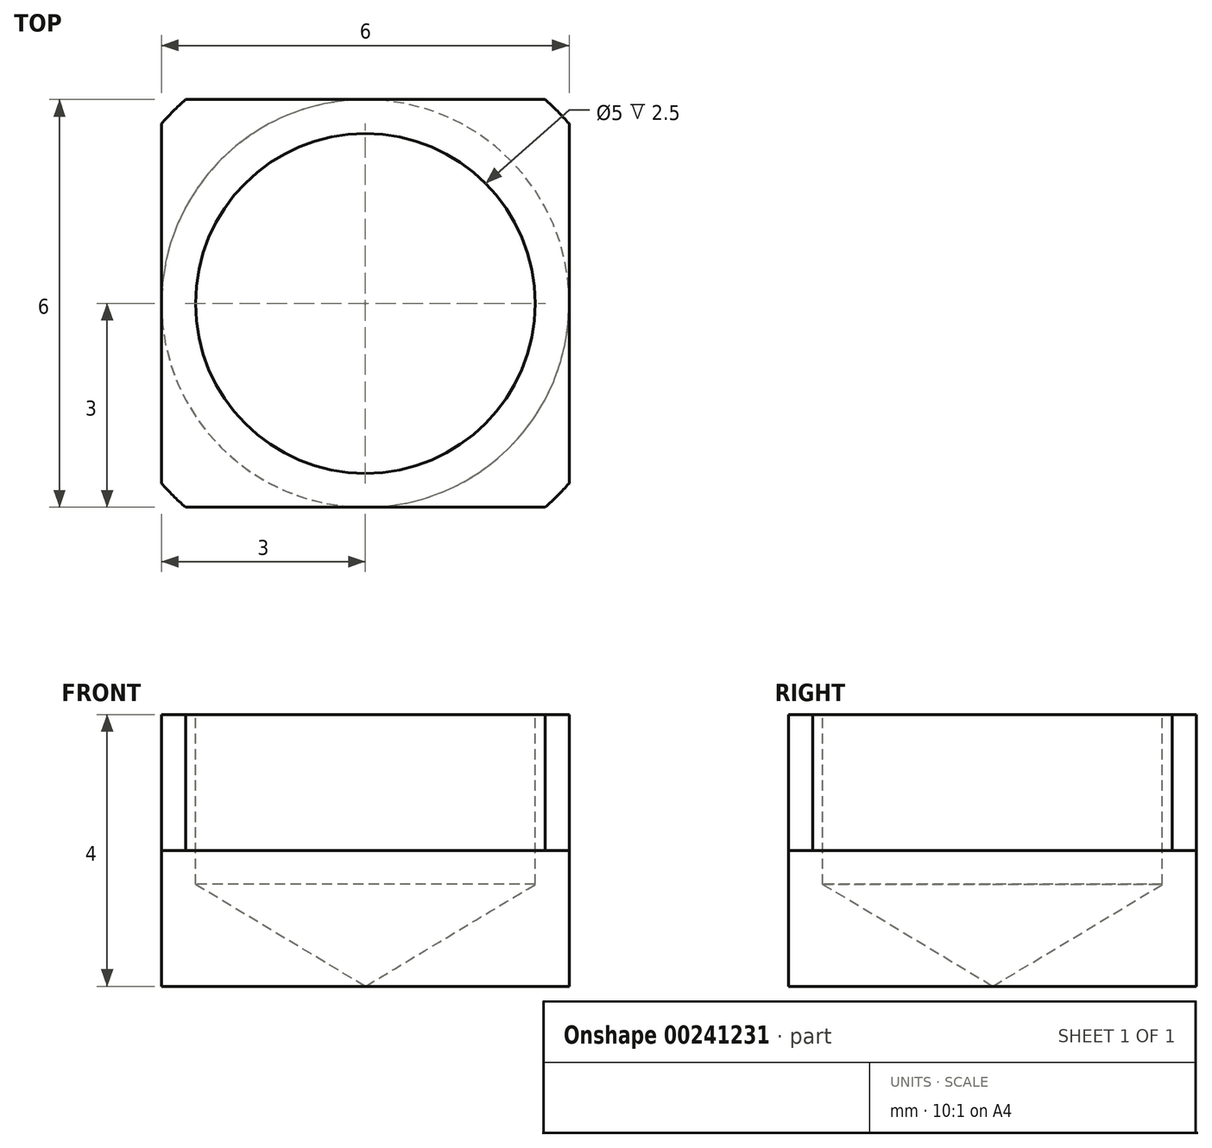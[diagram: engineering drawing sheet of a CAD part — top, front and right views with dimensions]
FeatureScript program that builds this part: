
annotation { "Feature Type Name" : "Feature", "Feature Type Description" : "" }
export const myFeature = defineFeature(function(context is Context, id is Id, definition is map)
    precondition{}
    {
        {
            var Q0;
            Q0=qCreatedBy(makeId("Top.planeOp"),FACE);
            var sketch = newSketch(context, id + "F0", { "sketchPlane" : qUnion([Q0])});
            skCircle(sketch, "E0", {"center": v(0, 0) * mm, "radius": 3 * mm});
            skSolve(sketch);
        }
        {
            var Q0;
            Q0 = qSketchRegion(id + "F0", true);
            extrude(context, id + "F1", {"entities" : qUnion([Q0]), "depth" : 2 * mm});
        }
        {
            var Q0;
            Q0=makeQuery(id+"F1.opExtrude","CAP_FACE",FACE,{"disambiguationData":[OSD([sQuery(id+"F0.wireOp",EDGE,"E0")])],"isStart":false});
            var sketch = newSketch(context, id + "F2", { "sketchPlane" : qUnion([Q0])});
            skCircle(sketch, "E1", {"center": v(0, 0) * mm, "radius": 4 * mm});
            skSolve(sketch);
        }
        {
            var Q0;
            Q0 = qSketchRegion(id + "F2", true);
            extrude(context, id + "F3", {"entities" : qUnion([Q0]), "operationType" : NewBodyOperationType.ADD, "depth" : 2 * mm});
        }
        {
            var Q0;
            Q0=makeQuery(id+"F3.opExtrude","CAP_FACE",FACE,{"disambiguationData":[OSD([sQuery(id+"F2.wireOp",EDGE,"E1")])],"isStart":false});
            var sketch = newSketch(context, id + "F4", { "sketchPlane" : qUnion([Q0])});
            skPoint(sketch, "E2", {"position": v(0, 0) * mm});
            skSolve(sketch);
        }
        {
            var Q0;
            Q0=makeQuery(id+"F3.opExtrude","CAP_FACE",FACE,{"disambiguationData":[OSD([sQuery(id+"F2.wireOp",EDGE,"E1")])],"isStart":false});
            var sketch = newSketch(context, id + "F5", { "sketchPlane" : qUnion([Q0])});
            skLineSegment(sketch, "E3.bottom", {"start": v(-3, 3) * mm, "end": v(3, 3) * mm});
            skLineSegment(sketch, "E3.top", {"start": v(-3, -3) * mm, "end": v(3, -3) * mm});
            skLineSegment(sketch, "E3.left", {"start": v(-3, 3) * mm, "end": v(-3, -3) * mm});
            skLineSegment(sketch, "E3.right", {"start": v(3, 3) * mm, "end": v(3, -3) * mm});
            skSolve(sketch);
        }
        {
            var Q0;
            Q0 = qSketchRegion(id + "F5", true);
            extrude(context, id + "F6", {"entities" : qUnion([Q0]), "operationType" : NewBodyOperationType.INTERSECT, "oppositeDirection" : true, "depth" : 25 * mm});
        }
        {
            var Q0;
            Q0=sQuery(id+"F4.wireOp",VERTEX,"E2");
            var Q1;
            Q1=makeQuery(id+"F1.opExtrude","SWEPT_BODY",BODY,{"disambiguationData":[OSD([sQuery(id+"F0.wireOp",EDGE,"E0")])]});
            hole(context, id + "F7", {"style" : HoleStyle.SIMPLE, "endStyle" : HoleEndStyle.BLIND, "holeDiameter" : 5 * mm, "holeDepth" : 2.5 * mm, "tappedDepth" : 12 * mm, "tapClearance" : 3, "locations" : qUnion([Q0]), "scope" : qUnion([Q1])});
        }
    });
